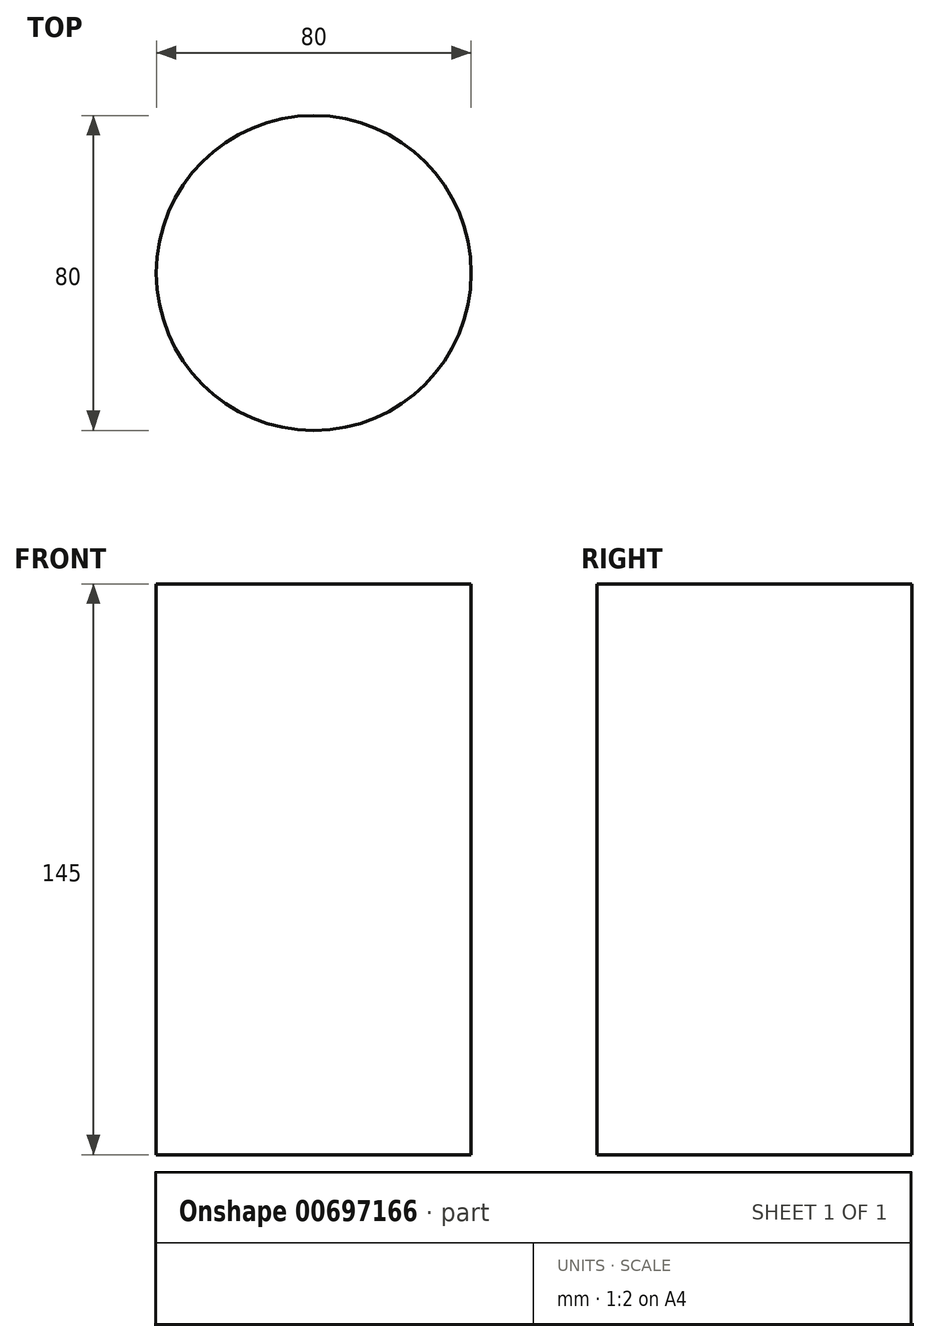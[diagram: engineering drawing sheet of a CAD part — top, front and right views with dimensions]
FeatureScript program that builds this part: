
annotation { "Feature Type Name" : "Feature", "Feature Type Description" : "" }
export const myFeature = defineFeature(function(context is Context, id is Id, definition is map)
    precondition{}
    {
        {
            var Q0;
            Q0=qCreatedBy(makeId("Top.planeOp"),FACE);
            var sketch = newSketch(context, id + "F0", { "sketchPlane" : qUnion([Q0])});
            skCircle(sketch, "E0", {"center": v(-1.62, 0) * mm, "radius": 40 * mm});
            skSolve(sketch);
        }
        {
            var Q0;
            Q0 = qSketchRegion(id + "F0", true);
            extrude(context, id + "F1", {"entities" : qUnion([Q0]), "depth" : 25 * mm, "offsetDistance" : 25 * mm});
        }
        {
            var Q0;
            Q0=makeQuery(id+"F0.imprint","IMPRINT",FACE,{"disambiguationData":[TD([[makeQuery(id+"F0.imprint","IMPRINT",EDGE,{"derivedFrom":sQuery(id+"F0.wireOp",EDGE,"E0")}),1.0]])]});
            extrude(context, id + "F2", {"entities" : qUnion([Q0]), "operationType" : NewBodyOperationType.ADD, "depth" : 145 * mm, "offsetDistance" : 25 * mm});
        }
        {
            var Q0;
            Q0=qCreatedBy(makeId("Right.planeOp"),FACE);
            cPlane(context, id + "F3", {"entities" : qUnion([Q0]), "cplaneType" : CPlaneType.OFFSET, "offset" : 33.4 * mm, "width" : 150 * mm, "height" : 150 * mm});
        }
    });
